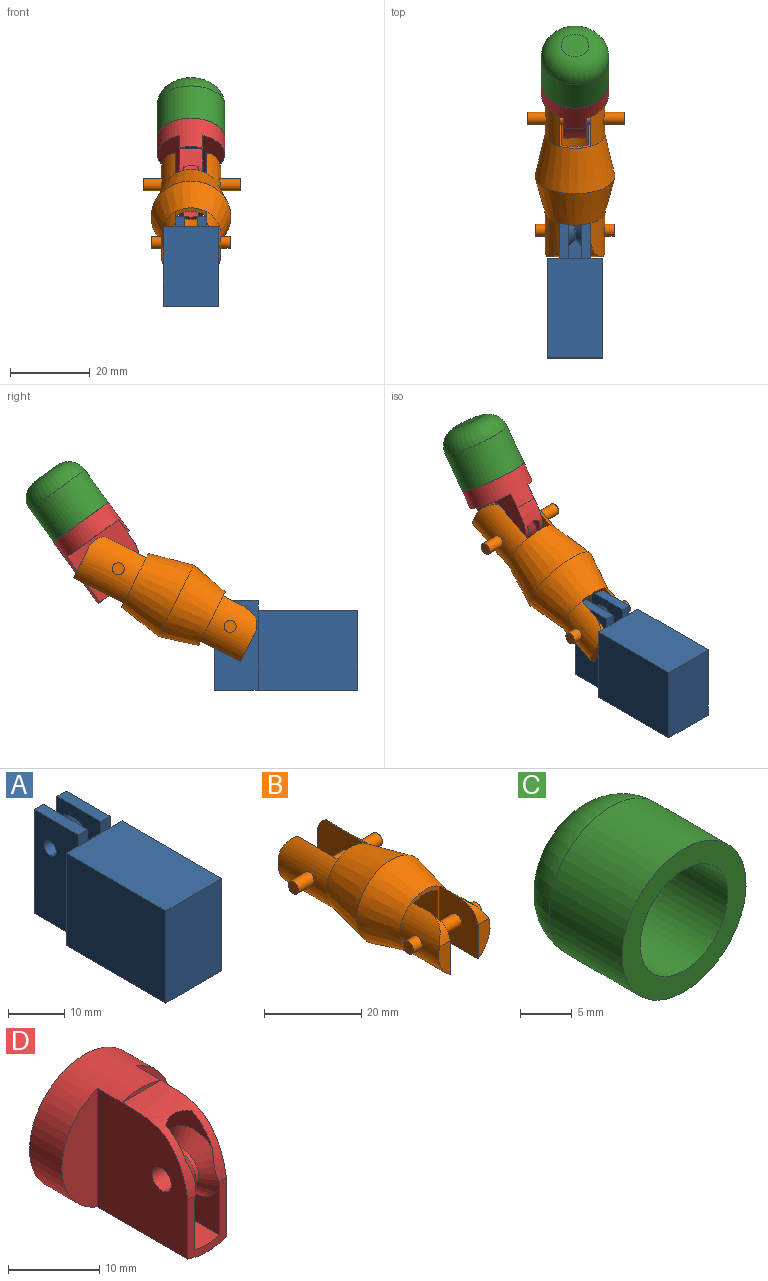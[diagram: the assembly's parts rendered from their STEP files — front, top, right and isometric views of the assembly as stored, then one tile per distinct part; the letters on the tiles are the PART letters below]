
ASSEMBLY  parts=4 mates=3
PART A: 22 faces, bbox 14x36x22.5 mm
  f0: plane 2.5x2.3mm, normal (0,-1,0), area 5.7mm2, adj f3,f4,f5,f13
  f1: plane 2.5x2.3mm, normal (0,-1,0), area 5.7mm2, adj f8,f9,f10,f13
  f2: plane 11x3.4mm, normal (0,0,1), area 37.4mm2, adj f3,f7,f8,f12
  f3: plane 12.7x11mm, normal (1,0,0), area 89.4mm2, adj f0,f2,f4,f7,f12,f20
  f4: plane 11x2.3mm, normal (0,0,1), area 25.3mm2, adj f0,f3,f5,f7
  f5: plane 22.5x11mm, normal (-1,0,0), area 240.4mm2, adj f0,f4,f6,f7,f17,f18
  f6: plane 36x14mm, normal (0,0,-1), area 438mm2, adj f5,f7,f10,f11,f14,f15,f16,f17
  f7: plane 22.5x8mm, normal (0,1,0), area 136.8mm2, adj f2,f3,f4,f5,f6,f8,f9,f10
  f8: plane 12.7x11mm, normal (-1,0,0), area 89.4mm2, adj f1,f2,f7,f9,f12,f21
  f9: plane 11x2.3mm, normal (0,0,1), area 25.3mm2, adj f1,f7,f8,f10
  f10: plane 22.5x11mm, normal (1,0,0), area 240.4mm2, adj f1,f6,f7,f9,f11,f18
  f11: plane 20x3mm, normal (0,1,0), area 60mm2, adj f6,f10,f13,f15
  f12: plane 10.2x3.4mm, normal (0,1,0), area 34.7mm2, adj f2,f3,f8,f13
  f13: plane 25x14mm, normal (0,0,1), area 350mm2, adj f0,f1,f11,f12,f14,f15,f16,f17
  f14: plane 25x20mm, normal (-1,0,0), area 500mm2, adj f6,f13,f16,f17
  f15: plane 25x20mm, normal (1,0,0), area 500mm2, adj f6,f11,f13,f16
  f16: plane 20x14mm, normal (0,-1,0), area 280mm2, adj f6,f13,f14,f15
  f17: plane 20x3mm, normal (0,1,0), area 60mm2, adj f5,f6,f13,f14
  f18: cylinder r=1.5mm len=8mm, axis (1,0,0), area 75.4mm2, adj f5,f10
  f19: cylinder r=2.5mm len=5mm, axis (1,0,0), area 6.3mm2, adj f20,f21
  f20: cone r=2.5mm half-angle=45deg, axis (-1,0,0), area 43.3mm2, adj f3,f19
  f21: cone r=2.5mm half-angle=45deg, axis (1,0,0), area 43.3mm2, adj f8,f19
PART B: 34 faces, bbox 24.5x46.8x20 mm
  f0: cylinder r=7.5mm len=12.69mm, axis (0,1,0), area 155.5mm2, adj f1,f10,f16,f19,f27
  f1: plane 12.69x11.3mm, normal (-1,0,0), area 130.8mm2, adj f0,f4,f16,f19,f26
  f2: plane 12.69x11.3mm, normal (1,0,0), area 130.8mm2, adj f3,f4,f17,f18,f26
  f3: cylinder r=7.5mm len=12.69mm, axis (0,1,0), area 155.5mm2, adj f2,f10,f17,f18,f25
  f4: plane 15x8mm, normal (0,-1,0), area 28.4mm2, adj f1,f2,f10,f20,f21,f22,f23
  f5: plane 14x12.8mm, normal (-1,0,0), area 167.8mm2, adj f6,f9,f12,f15,f29
  f6: cylinder r=7.5mm len=14mm, axis (0,-1,0), area 200.5mm2, adj f5,f11,f12,f15,f32
  f7: cylinder r=7.5mm len=14mm, axis (0,-1,0), area 200.5mm2, adj f8,f11,f13,f14,f31
  f8: plane 14x12.8mm, normal (1,0,0), area 167.8mm2, adj f7,f9,f13,f14,f29
  f9: plane 15x8mm, normal (0,1,0), area 28.4mm2, adj f5,f8,f11,f20,f21,f22,f23
  f10: cone r=7.5mm half-angle=14deg, axis (0,1,0), area 566.7mm2, adj f0,f3,f4,f11
  f11: cone r=10mm half-angle=12.3deg, axis (0,-1,0), area 647mm2, adj f6,f7,f9,f10
  f12: plane 9.38x3.5mm, normal (0,1,0), area 25.7mm2, adj f5,f6,f15
  f13: plane 9.38x3.5mm, normal (0,1,0), area 25.7mm2, adj f7,f8,f14
  f14: extruded ~3.31x2.86mm, area 6.5mm2, adj f7,f8,f13
  f15: extruded ~3.31x2.86mm, area 6.5mm2, adj f5,f6,f12
  f16: plane 8.62x3.5mm, normal (0,-1,0), area 23.4mm2, adj f0,f1,f19
  f17: plane 8.62x3.5mm, normal (0,-1,0), area 23.4mm2, adj f2,f3,f18
  f18: extruded ~5.65x4.07mm, area 10.5mm2, adj f2,f3,f17
  f19: extruded ~5.65x4.07mm, area 10.5mm2, adj f0,f1,f16
  f20: cylinder r=6.5mm len=21.5mm, axis (0,1,0), area 157.2mm2, adj f4,f9,f21,f23
  f21: plane 21.5x11mm, normal (-1,0,0), area 236.4mm2, adj f4,f9,f20,f22
  f22: cylinder r=6.5mm len=21.5mm, axis (0,1,0), area 157.2mm2, adj f4,f9,f21,f23
  f23: plane 21.5x11mm, normal (1,0,0), area 236.4mm2, adj f4,f9,f20,f22
  f24: plane 3x3mm, normal (-1,0,0), area 7.1mm2, adj f25
  f25: cylinder r=1.5mm len=3mm, axis (-1,0,0), area 24.4mm2, adj f3,f24
  f26: cylinder r=1.5mm len=8mm, axis (-1,0,0), area 75.4mm2, adj f1,f2
  f27: cylinder r=1.5mm len=3mm, axis (-1,0,0), area 22.6mm2, adj f0,f28
  f28: plane 3x3mm, normal (1,0,0), area 7.1mm2, adj f27
  f29: cylinder r=1.5mm len=8mm, axis (-1,0,0), area 75.4mm2, adj f5,f8
  f30: plane 3x3mm, normal (-1,0,0), area 7.1mm2, adj f31
  f31: cylinder r=1.5mm len=4.83mm, axis (-1,0,0), area 43.4mm2, adj f7,f30
  f32: cylinder r=1.5mm len=5.33mm, axis (-1,0,0), area 48.2mm2, adj f6,f33
  f33: plane 3x3mm, normal (1,0,0), area 7.1mm2, adj f32
PART C: 7 faces, bbox 17x15x17 mm
  f0: cylinder r=8.5mm len=17mm, axis (0,-1,0), area 534.1mm2, adj f2,f3
  f1: plane 7x7mm, normal (0,1,0), area 38.5mm2, adj f3
  f2: plane 17x17mm, normal (0,-1,0), area 113.9mm2, adj f0,f4
  f3: torus R=3.5mm, axis (0,1,0), area 329.8mm2, adj f0,f1
  f4: cylinder r=6mm len=12mm, axis (0,-1,0), area 377mm2, adj f2,f6
  f5: plane 7x7mm, normal (0,-1,0), area 38.5mm2, adj f6
  f6: torus R=3.5mm, axis (0,1,0), area 125.6mm2, adj f4,f5
PART D: 20 faces, bbox 17x19.3x17 mm
  f0: plane 15.91x14mm, normal (-1,0,0), area 201.5mm2, adj f1,f2,f3,f8,f9
  f1: cylinder r=8.5mm len=19mm, axis (0,-1,0), area 376.5mm2, adj f0,f2,f3,f4,f5,f6,f7
  f2: plane 8.54x6.04mm, normal (0,-1,0), area 20.4mm2, adj f0,f1,f6,f8,f11,f12,f13,f16
  f3: plane 15.91x5.5mm, normal (0,-1,0), area 63.6mm2, adj f0,f1
  f4: plane 17x17mm, normal (0,1,0), area 220.7mm2, adj f1,f18,f19
  f5: plane 15.91x5.5mm, normal (0,-1,0), area 63.6mm2, adj f1,f6
  f6: plane 15.91x14mm, normal (1,0,0), area 201.5mm2, adj f1,f2,f5,f8,f9
  f7: plane 6x0.55mm, normal (0,-1,0), area 2.2mm2, adj f1,f8
  f8: extruded ~10.15x7.95mm, area 53mm2, adj f0,f2,f6,f7,f10,f11,f12,f16
  f9: cylinder r=1.5mm len=6mm, axis (1,0,0), area 56.5mm2, adj f0,f6
  f10: cylinder r=7.5mm len=11.59mm, axis (0,-1,0), area 45mm2, adj f8,f11,f12,f14
  f11: plane 16x14.49mm, normal (1,0,0), area 166mm2, adj f2,f8,f10,f13,f14,f17
  f12: plane 16x14.49mm, normal (-1,0,0), area 166mm2, adj f2,f8,f10,f13,f14,f16
  f13: cylinder r=7.5mm len=16mm, axis (0,-1,0), area 64.8mm2, adj f2,f11,f12,f14
  f14: plane 15x4mm, normal (0,-1,0), area 53mm2, adj f10,f11,f12,f13,f18,f19
  f15: cylinder r=2.5mm len=5mm, axis (-1,0,0), area 7.9mm2, adj f16,f17
  f16: cone r=2.5mm half-angle=45deg, axis (1,0,0), area 50.6mm2, adj f2,f8,f12,f15
  f17: cone r=2.5mm half-angle=45deg, axis (-1,0,0), area 50.6mm2, adj f2,f8,f11,f15
  f18: cylinder r=1mm len=3mm, axis (0,-1,0), area 18.8mm2, adj f4,f14
  f19: cylinder r=1mm len=3mm, axis (0,-1,0), area 18.8mm2, adj f4,f14
PLACE A t=(17.68,-8.33,-13.04)mm fixed
PLACE B rot(axis=(1,0,0),26.6deg) t=(17.68,-1.6,-9.56)mm
PLACE C rot(axis=(1,0,0),53.9deg) t=(17.68,12.73,-14.5)mm
PLACE D rot(axis=(1,0,0),53.9deg) t=(17.68,12.73,-14.5)mm
MATE revolute A.f18 <-> B.f25  axis (1,0,0) through (21.68,-12.33,2.96)mm
MATE fastened D.f1 <-> C.f0  axis (0,0.59,0.81) through (17.68,25.08,29.09)mm
MATE revolute B.f29 <-> D.f15  axis (-1,0,0) through (17.68,15.7,17.39)mm
